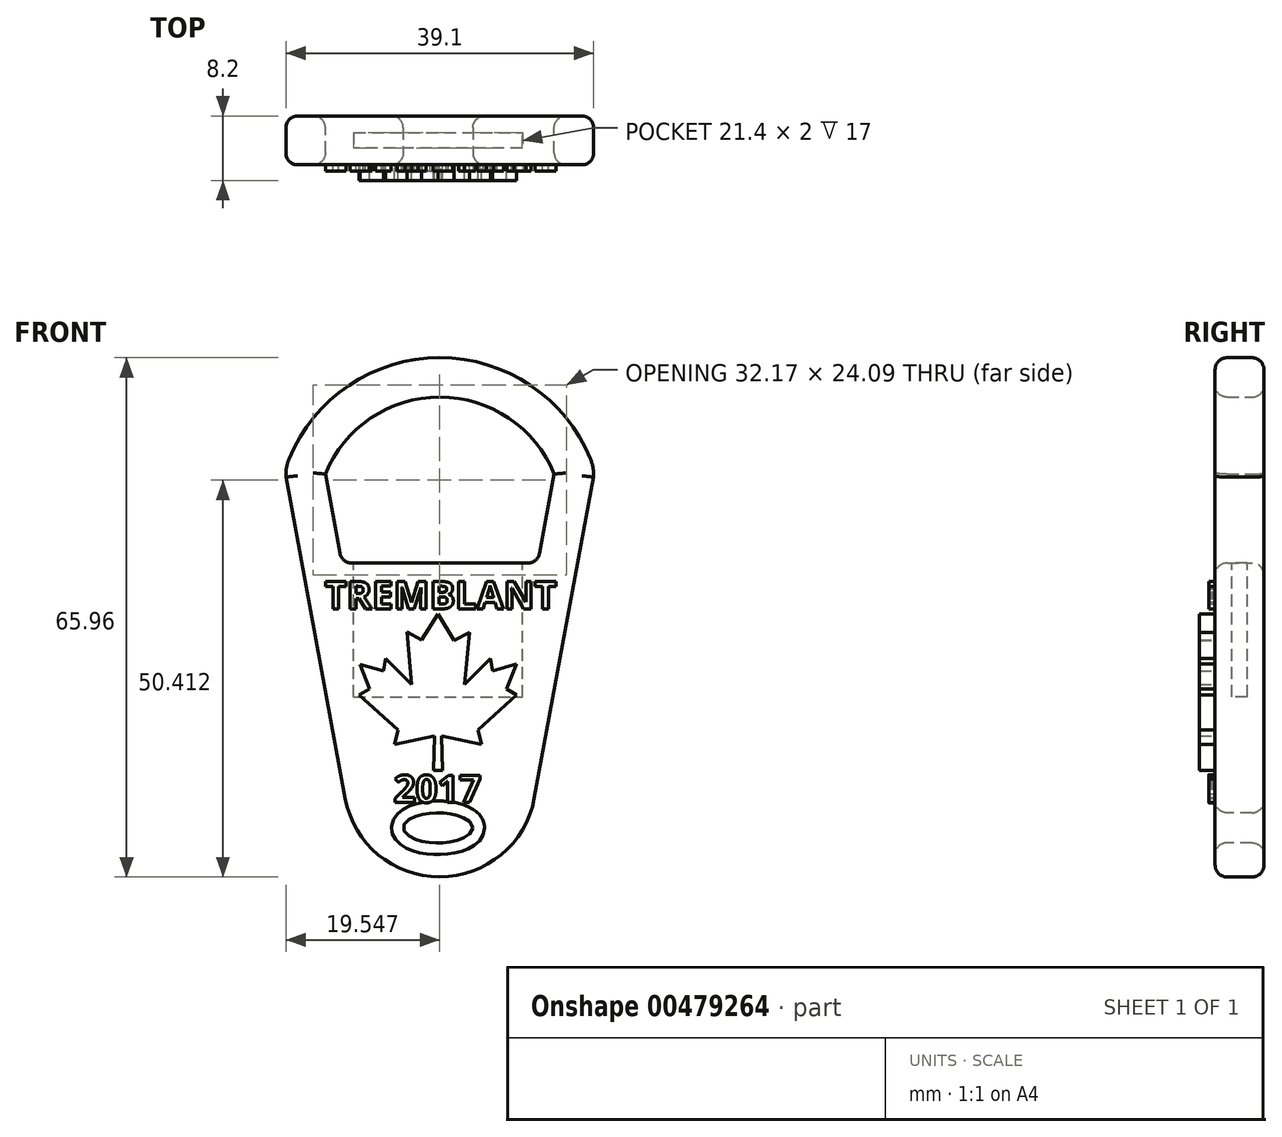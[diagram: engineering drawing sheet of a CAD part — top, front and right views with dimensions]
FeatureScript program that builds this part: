
annotation { "Feature Type Name" : "Feature", "Feature Type Description" : "" }
export const myFeature = defineFeature(function(context is Context, id is Id, definition is map)
    precondition{}
    {
        {
            var Q0;
            Q0=qCreatedBy(makeId("Front.planeOp"),FACE);
            var sketch = newSketch(context, id + "F0", { "sketchPlane" : qUnion([Q0])});
            skLineSegment(sketch, "E0", {"start": v(0.22, 53.5) * mm, "end": v(0.22, -27.22) * mm, "construction": true});
            skLineSegment(sketch, "E1", {"start": v(19.76, 12.33) * mm, "end": v(12.22, -28.48) * mm});
            skLineSegment(sketch, "E2.MirrorCS", {"start": v(-19.33, 12.33) * mm, "end": v(-11.78, -28.48) * mm});
            skLineSegment(sketch, "E3.0", {"start": v(-14.31, 12.71) * mm, "end": v(-12.22, 1.4) * mm});
            skLineSegment(sketch, "E3.3", {"start": v(14.75, 12.71) * mm, "end": v(12.66, 1.4) * mm});
            skLineSegment(sketch, "E4", {"start": v(-12.22, 1.4) * mm, "end": v(12.66, 1.4) * mm});
            skPoint(sketch, "E5", {"position": v(0.22, 20.6) * mm});
            skPoint(sketch, "E6", {"position": v(-14.31, 12.71) * mm});
            skPoint(sketch, "E7.MirrorP", {"position": v(14.75, 12.71) * mm});
            skArc(sketch, "E8", {"start": v(14.75, 12.71) * mm, "mid": v(0.22, 22.5) * mm, "end": v(-14.31, 12.71) * mm});
            skArc(sketch, "E9.0", {"start": v(19.62, 13.97) * mm, "mid": v(0.56, 27.5) * mm, "end": v(-18.94, 14.6) * mm});
            skArc(sketch, "E10", {"start": v(-18.94, 14.6) * mm, "mid": v(-19.26, 13.5) * mm, "end": v(-19.33, 12.33) * mm});
            skArc(sketch, "E11.MirrorCS", {"start": v(19.38, 14.6) * mm, "mid": v(19.7, 13.5) * mm, "end": v(19.76, 12.33) * mm});
            skPoint(sketch, "E12.orphan", {"position": v(-21.9, 26.19) * mm});
            skPoint(sketch, "E13.orphan", {"position": v(22.32, 26.19) * mm});
            skPoint(sketch, "E14.MirrorCS.start.orphan", {"position": v(0.22, 25.6) * mm});
            skArc(sketch, "E15", {"start": v(-11.78, -28.48) * mm, "mid": v(0.22, -38.46) * mm, "end": v(12.22, -28.48) * mm});
            skPoint(sketch, "E16.MirrorCS.end.orphan", {"position": v(0.22, -28.48) * mm});
            skPoint(sketch, "E16.MirrorCS.start.orphan", {"position": v(-11.78, -28.48) * mm});
            skLineSegment(sketch, "E17", {"start": v(-11.78, -28.48) * mm, "end": v(12.22, -28.48) * mm, "construction": true});
            skSolve(sketch);
        }
        {
            var Q0;
            Q0=qSketchRegion(id+"F0",true);
            extrude(context, id + "F1", {"entities" : qUnion([Q0]), "depth" : 6.2 * mm});
        }
        {
            var Q0;
            Q0=makeQuery(id+"F1.opExtrude","CAP_FACE",FACE,{"disambiguationData":[OSD([sQuery(id+"F0.wireOp",EDGE,"E1"),sQuery(id+"F0.wireOp",EDGE,"E2.MirrorCS"),sQuery(id+"F0.wireOp",EDGE,"E3.0"),sQuery(id+"F0.wireOp",EDGE,"E3.3"),sQuery(id+"F0.wireOp",EDGE,"E4"),sQuery(id+"F0.wireOp",EDGE,"E8"),sQuery(id+"F0.wireOp",EDGE,"E9.0"),sQuery(id+"F0.wireOp",EDGE,"E10"),sQuery(id+"F0.wireOp",EDGE,"E11.MirrorCS"),sQuery(id+"F0.wireOp",EDGE,"E15")])],"isStart":false});
            var sketch = newSketch(context, id + "F2", { "sketchPlane" : qUnion([Q0])});
            skEllipse(sketch, "E18", {"center": v(0, -32.22) * mm, "majorRadius": 4.42 * mm, "minorRadius": 1.9 * mm, "majorAxis": v(1, 0)});
            skSolve(sketch);
        }
        {
            var Q0;
            Q0=makeQuery(id+"F2.imprint","IMPRINT",FACE,{"disambiguationData":[TD([[makeQuery(id+"F2.imprint","IMPRINT",EDGE,{"derivedFrom":sQuery(id+"F2.wireOp",EDGE,"E18")}),1.0]])]});
            extrude(context, id + "F3", {"entities" : qUnion([Q0]), "operationType" : NewBodyOperationType.REMOVE, "oppositeDirection" : true, "depth" : 6.5 * mm});
        }
        {
            var Q0;
            Q0=makeQuery(id+"F1.opExtrude","SWEPT_FACE",FACE,{"disambiguationData":[OSD([sQuery(id+"F0.wireOp",EDGE,"E4")])]});
            var sketch = newSketch(context, id + "F4", { "sketchPlane" : qUnion([Q0])});
            skLineSegment(sketch, "E19", {"start": v(0, -2.1) * mm, "end": v(10.7, -2.1) * mm});
            skLineSegment(sketch, "E20.0", {"start": v(0, -4.1) * mm, "end": v(10.7, -4.1) * mm});
            skLineSegment(sketch, "E21", {"start": v(10.7, -2.1) * mm, "end": v(10.7, -4.1) * mm});
            skLineSegment(sketch, "E22", {"start": v(0, -2.1) * mm, "end": v(0, -4.1) * mm, "construction": true});
            skLineSegment(sketch, "E23.MirrorCS", {"start": v(0, -2.1) * mm, "end": v(-10.7, -2.1) * mm});
            skLineSegment(sketch, "E24.MirrorCS", {"start": v(-10.7, -2.1) * mm, "end": v(-10.7, -4.1) * mm});
            skLineSegment(sketch, "E25.MirrorCS", {"start": v(0, -4.1) * mm, "end": v(-10.7, -4.1) * mm});
            skSolve(sketch);
        }
        {
            var Q0;
            Q0=makeQuery(id+"F4.imprint","IMPRINT",FACE,{"disambiguationData":[TD([[makeQuery(id+"F4.imprint","IMPRINT",EDGE,{"derivedFrom":sQuery(id+"F4.wireOp",EDGE,"E19")}),-1.0]])]});
            extrude(context, id + "F5", {"entities" : qUnion([Q0]), "operationType" : NewBodyOperationType.REMOVE, "oppositeDirection" : true, "depth" : 17 * mm});
        }
        {
            var Q0;
            Q0=makeQuery(id+"F1.opExtrude","SWEPT_EDGE",EDGE,{"disambiguationData":[OSD([sQuery(id+"F0.wireOp",EDGE,"E3.0"),sQuery(id+"F0.wireOp",EDGE,"E4")])]});
            var Q1;
            Q1=makeQuery(id+"F1.opExtrude","SWEPT_EDGE",EDGE,{"disambiguationData":[OSD([sQuery(id+"F0.wireOp",EDGE,"E3.3"),sQuery(id+"F0.wireOp",EDGE,"E4")])]});
            var Q2;
            Q2=makeQuery(id+"F1.opExtrude","CAP_FACE",FACE,{"disambiguationData":[OSD([sQuery(id+"F0.wireOp",EDGE,"E1"),sQuery(id+"F0.wireOp",EDGE,"E2.MirrorCS"),sQuery(id+"F0.wireOp",EDGE,"E3.0"),sQuery(id+"F0.wireOp",EDGE,"E3.3"),sQuery(id+"F0.wireOp",EDGE,"E4"),sQuery(id+"F0.wireOp",EDGE,"E8"),sQuery(id+"F0.wireOp",EDGE,"E9.0"),sQuery(id+"F0.wireOp",EDGE,"E10"),sQuery(id+"F0.wireOp",EDGE,"E11.MirrorCS"),sQuery(id+"F0.wireOp",EDGE,"E15")])],"isStart":false});
            var Q3;
            Q3=makeQuery(id+"F1.opExtrude","CAP_FACE",FACE,{"disambiguationData":[OSD([sQuery(id+"F0.wireOp",EDGE,"E1"),sQuery(id+"F0.wireOp",EDGE,"E2.MirrorCS"),sQuery(id+"F0.wireOp",EDGE,"E3.0"),sQuery(id+"F0.wireOp",EDGE,"E3.3"),sQuery(id+"F0.wireOp",EDGE,"E4"),sQuery(id+"F0.wireOp",EDGE,"E8"),sQuery(id+"F0.wireOp",EDGE,"E9.0"),sQuery(id+"F0.wireOp",EDGE,"E10"),sQuery(id+"F0.wireOp",EDGE,"E11.MirrorCS"),sQuery(id+"F0.wireOp",EDGE,"E15")])],"isStart":true});
            fillet(context, id + "F6", {"entities" : qUnion([Q0, Q1, Q2, Q3]), "radius" : 1.5 * mm, "tangentPropagation" : true, "allowEdgeOverflow" : false});
        }
        {
            var Q0;
            Q0=makeQuery(id+"F1.opExtrude","CAP_FACE",FACE,{"disambiguationData":[OSD([sQuery(id+"F0.wireOp",EDGE,"E1"),sQuery(id+"F0.wireOp",EDGE,"E2.MirrorCS"),sQuery(id+"F0.wireOp",EDGE,"E3.0"),sQuery(id+"F0.wireOp",EDGE,"E3.3"),sQuery(id+"F0.wireOp",EDGE,"E4"),sQuery(id+"F0.wireOp",EDGE,"E8"),sQuery(id+"F0.wireOp",EDGE,"E9.0"),sQuery(id+"F0.wireOp",EDGE,"E10"),sQuery(id+"F0.wireOp",EDGE,"E11.MirrorCS"),sQuery(id+"F0.wireOp",EDGE,"E15")])],"isStart":false});
            var sketch = newSketch(context, id + "F7", { "sketchPlane" : qUnion([Q0])});
            skText(sketch, "E26", { "text": "TREMBLANT", "fontName": "OpenSans-Bold.ttf"});
            skPoint(sketch, "E26.secondSnap0", {"position": v(14.5, -7.85) * mm});
            skText(sketch, "E27", { "text": "2017", "fontName": "OpenSans-Bold.ttf"});
            const initialGuessF7  = {"E26": [-0.0144, -0.0044, 1, 0, 0.0035], "E27": [-0.00563, -0.02901, 1, 0, 0.0035]};
            skSetInitialGuess(sketch, initialGuessF7);
            skSolve(sketch);
        }
        {
            var Q0;
            Q0 = qSketchRegion(id + "F7", true);
            extrude(context, id + "F8", {"entities" : qUnion([Q0]), "operationType" : NewBodyOperationType.ADD, "depth" : .8 * mm, "offsetDistance" : 25 * mm});
        }
        {
            var Q0;
            {var subQ0=sQuery(id+"F0.wireOp",EDGE,"E11.MirrorCS");var subQ1=sQuery(id+"F0.wireOp",EDGE,"E2.MirrorCS");var subQ2=sQuery(id+"F0.wireOp",EDGE,"E1");var subQ3=sQuery(id+"F0.wireOp",EDGE,"E4");var subQ4=sQuery(id+"F0.wireOp",EDGE,"E3.3");var subQ5=sQuery(id+"F0.wireOp",EDGE,"E3.0");var subQ6=sQuery(id+"F0.wireOp",EDGE,"E15");var subQ7=sQuery(id+"F0.wireOp",EDGE,"E8");var subQ8=sQuery(id+"F0.wireOp",EDGE,"E9.0");var subQ9=sQuery(id+"F0.wireOp",EDGE,"E10");Q0=makeQuery(id+"F8.boolean.opBoolean","SPLIT",FACE,{"disambiguationData":[TD([makeQuery(id+"F6.opFillet","BLEND_FACE",FACE,{"disambiguationData":[OSD([sQuery(id+"F2.wireOp",EDGE,"E18")])]})])],"derivedFrom":makeQuery(id+"F1.opExtrude","CAP_FACE",FACE,{"disambiguationData":[OSD([subQ2,subQ1,subQ5,subQ4,subQ3,subQ7,subQ8,subQ9,subQ0,subQ6])],"isStart":false})});}
            var sketch = newSketch(context, id + "F9", { "sketchPlane" : qUnion([Q0])});
            skLineSegment(sketch, "E28", {"start": v(-10, -15.34) * mm, "end": v(-5.07, -19.81) * mm});
            skLineSegment(sketch, "E29", {"start": v(-5.07, -19.81) * mm, "end": v(-5.53, -21.64) * mm});
            skLineSegment(sketch, "E30", {"start": v(-5.53, -21.64) * mm, "end": v(-0.45, -20.57) * mm});
            skLineSegment(sketch, "E31", {"start": v(-0.45, -20.57) * mm, "end": v(-0.55, -24.96) * mm});
            skLineSegment(sketch, "E32", {"start": v(-0.55, -24.96) * mm, "end": v(0.56, -24.96) * mm});
            skLineSegment(sketch, "E33", {"start": v(0.56, -24.96) * mm, "end": v(0.45, -20.57) * mm});
            skLineSegment(sketch, "E34", {"start": v(0.45, -20.57) * mm, "end": v(5.52, -21.63) * mm});
            skLineSegment(sketch, "E35", {"start": v(5.52, -21.63) * mm, "end": v(5.07, -19.82) * mm});
            skLineSegment(sketch, "E36", {"start": v(5.07, -19.82) * mm, "end": v(10, -15.33) * mm});
            skLineSegment(sketch, "E37", {"start": v(10, -15.33) * mm, "end": v(8.7, -14.6) * mm});
            skLineSegment(sketch, "E38", {"start": v(8.7, -14.6) * mm, "end": v(9.95, -11.41) * mm});
            skLineSegment(sketch, "E39", {"start": v(9.95, -11.41) * mm, "end": v(6.93, -12.3) * mm});
            skLineSegment(sketch, "E40", {"start": v(6.93, -12.3) * mm, "end": v(6.67, -10.71) * mm});
            skLineSegment(sketch, "E41", {"start": v(6.67, -10.71) * mm, "end": v(3.35, -14) * mm});
            skLineSegment(sketch, "E42", {"start": v(3.35, -14) * mm, "end": v(3.99, -7.4) * mm});
            skLineSegment(sketch, "E43", {"start": v(3.99, -7.4) * mm, "end": v(2.04, -8.44) * mm});
            skLineSegment(sketch, "E44", {"start": v(2.04, -8.44) * mm, "end": v(0, -5.04) * mm});
            skLineSegment(sketch, "E45", {"start": v(0, -5.04) * mm, "end": v(-2.1, -8.39) * mm});
            skLineSegment(sketch, "E46", {"start": v(-2.1, -8.39) * mm, "end": v(-3.95, -7.33) * mm});
            skLineSegment(sketch, "E47", {"start": v(-3.95, -7.33) * mm, "end": v(-3.35, -14) * mm});
            skLineSegment(sketch, "E48", {"start": v(-3.35, -14) * mm, "end": v(-6.64, -10.71) * mm});
            skLineSegment(sketch, "E49", {"start": v(-6.64, -10.71) * mm, "end": v(-6.92, -12.28) * mm});
            skLineSegment(sketch, "E50", {"start": v(-6.92, -12.28) * mm, "end": v(-9.89, -11.45) * mm});
            skLineSegment(sketch, "E51", {"start": v(-9.89, -11.45) * mm, "end": v(-8.72, -14.57) * mm});
            skLineSegment(sketch, "E52", {"start": v(-8.72, -14.57) * mm, "end": v(-10, -15.34) * mm});
            skSolve(sketch);
        }
        {
            var Q0;
            Q0 = qSketchRegion(id + "F9", true);
            extrude(context, id + "F10", {"entities" : qUnion([Q0]), "operationType" : NewBodyOperationType.ADD, "depth" : 2 * mm, "offsetDistance" : 25 * mm});
        }
    });
